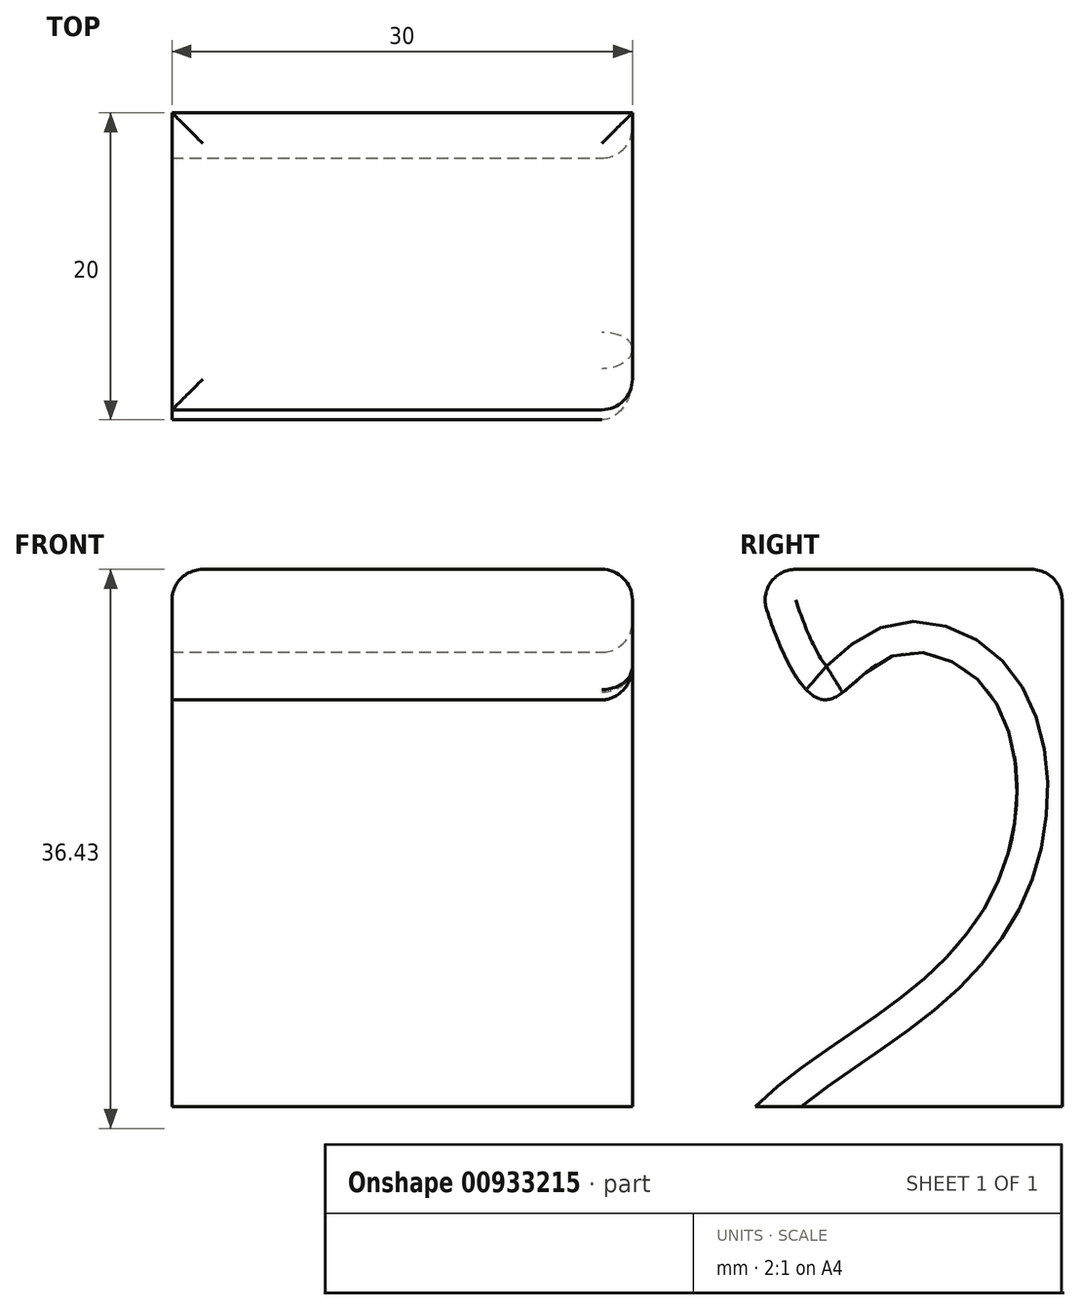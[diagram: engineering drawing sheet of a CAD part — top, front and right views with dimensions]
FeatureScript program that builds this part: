
annotation { "Feature Type Name" : "Feature", "Feature Type Description" : "" }
export const myFeature = defineFeature(function(context is Context, id is Id, definition is map)
    precondition{}
    {
        {
            var Q0;
            Q0=qCreatedBy(makeId("Top.planeOp"),FACE);
            var sketch = newSketch(context, id + "F0", { "sketchPlane" : qUnion([Q0])});
            skLineSegment(sketch, "E0.bottom", {"start": v(15, -10) * mm, "end": v(-15, -10) * mm});
            skLineSegment(sketch, "E0.top", {"start": v(15, 10) * mm, "end": v(-15, 10) * mm});
            skLineSegment(sketch, "E0.left", {"start": v(15, -10) * mm, "end": v(15, 10) * mm});
            skLineSegment(sketch, "E0.right", {"start": v(-15, -10) * mm, "end": v(-15, 10) * mm});
            skPoint(sketch, "E0.middle", {"position": v(0, 0) * mm});
            skSolve(sketch);
        }
        {
            var Q0;
            Q0=makeQuery(id+"F0.imprint","IMPRINT",FACE,{"disambiguationData":[TD([[makeQuery(id+"F0.imprint","IMPRINT",EDGE,{"derivedFrom":sQuery(id+"F0.wireOp",EDGE,"E0.bottom")}),-1.0]])]});
            extrude(context, id + "F1", {"entities" : qUnion([Q0]), "depth" : 25 * mm, "offsetDistance" : 25 * mm});
        }
        {
            var Q0;
            Q0=makeQuery(id+"F1.opExtrude","CAP_FACE",FACE,{"disambiguationData":[OSD([sQuery(id+"F0.wireOp",EDGE,"E0.bottom"),sQuery(id+"F0.wireOp",EDGE,"E0.top"),sQuery(id+"F0.wireOp",EDGE,"E0.left"),sQuery(id+"F0.wireOp",EDGE,"E0.right")])],"isStart":false});
            extrude(context, id + "F2", {"entities" : qUnion([Q0]), "operationType" : NewBodyOperationType.ADD, "depth" : 10 * mm, "offsetDistance" : 25 * mm});
        }
        {
            var Q0;
            {var subQ0=sQuery(id+"F0.wireOp",EDGE,"E0.right");Q0=makeQuery(id+"F2.boolean.opBoolean","MERGE",FACE,{"derivedFrom":[makeQuery(id+"F1.opExtrude","SWEPT_FACE",FACE,{"disambiguationData":[OSD([subQ0])]}),makeQuery(id+"F2.opExtrude","SWEPT_FACE",FACE,{"disambiguationData":[OSD([subQ0])]})]});}
            var sketch = newSketch(context, id + "F3", { "sketchPlane" : qUnion([Q0])});
            skFitSpline(sketch, "E1", {"points": [v(10, 35) * mm, v(5.45, 26.5) * mm, v(1.18, 29.31) * mm, v(-5.31, 26.89) * mm, v(-6.18, 15.54) * mm, v(1, 6.72) * mm, v(10, 0) * mm], "startDerivative": vector(-19.56, -77.92) * mm, "endDerivative": vector(42.87, -42.57) * mm});
            skSolve(sketch);
        }
        {
            var Q0;
            Q0=makeQuery(id+"F3.imprint","IMPRINT",FACE,{"disambiguationData":[TD([[makeQuery(id+"F3.imprint","IMPRINT",EDGE,{"derivedFrom":sQuery(id+"F3.wireOp",EDGE,"E1")}),1.0]])]});
            extrude(context, id + "F4", {"entities" : qUnion([Q0]), "operationType" : NewBodyOperationType.REMOVE, "endBound" : BoundingType.THROUGH_ALL, "oppositeDirection" : true, "depth" : 25 * mm, "offsetDistance" : 25 * mm});
        }
        {
            var Q0;
            Q0=makeQuery(id+"F2.opExtrude","CAP_FACE",FACE,{"disambiguationData":[OSD([sQuery(id+"F0.wireOp",EDGE,"E0.bottom"),sQuery(id+"F0.wireOp",EDGE,"E0.top"),sQuery(id+"F0.wireOp",EDGE,"E0.left"),sQuery(id+"F0.wireOp",EDGE,"E0.right")])],"isStart":false});
            var Q1;
            Q1=makeQuery(id+"F4.boolean.opBoolean","COPY",EDGE,{"derivedFrom":makeQuery(id+"F4.opExtrude","CAP_EDGE",EDGE,{"disambiguationData":[OSD([sQuery(id+"F3.wireOp",EDGE,"E1")])],"isStart":true})});
            var Q2;
            {var subQ0=sQuery(id+"F0.wireOp",EDGE,"E0.left");Q2=makeQuery(id+"F4.boolean.opBoolean","INTERSECT",EDGE,{"derivedFrom":[makeQuery(id+"F2.boolean.opBoolean","MERGE",FACE,{"derivedFrom":[makeQuery(id+"F1.opExtrude","SWEPT_FACE",FACE,{"disambiguationData":[OSD([subQ0])]}),makeQuery(id+"F2.opExtrude","SWEPT_FACE",FACE,{"disambiguationData":[OSD([subQ0])]})]}),makeQuery(id+"F4.opExtrude","SWEPT_FACE",FACE,{"disambiguationData":[OSD([sQuery(id+"F3.wireOp",EDGE,"E1")])]})]});}
            fillet(context, id + "F5", {"entities" : qUnion([Q0, Q1, Q2]), "radius" : 2 * mm, "tangentPropagation" : true, "allowEdgeOverflow" : false});
        }
    });
